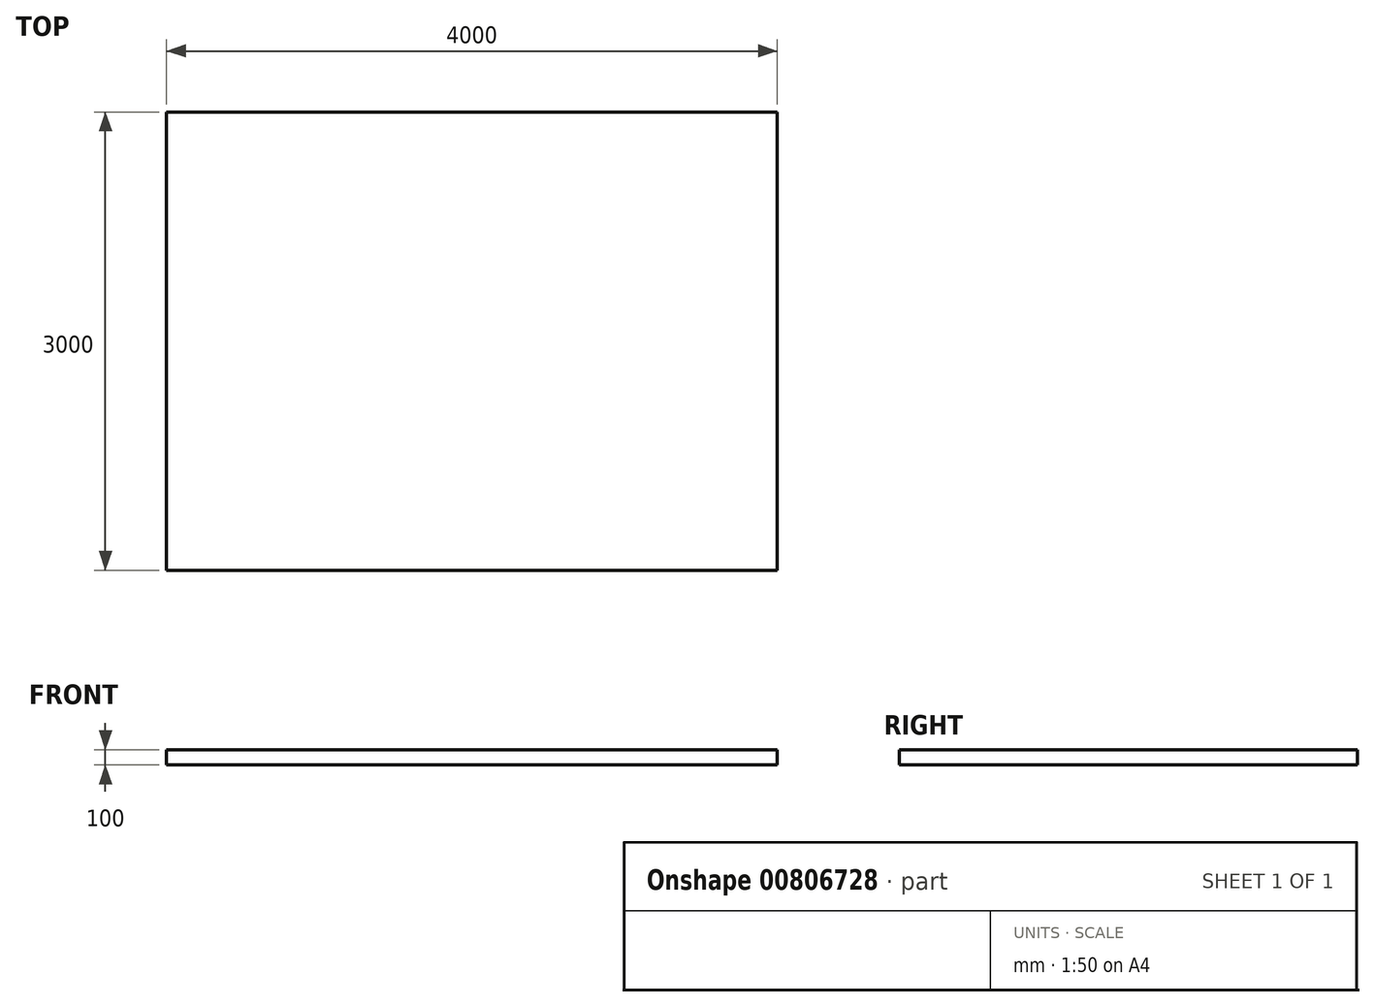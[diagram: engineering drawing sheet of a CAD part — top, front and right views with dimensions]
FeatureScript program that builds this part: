
annotation { "Feature Type Name" : "Feature", "Feature Type Description" : "" }
export const myFeature = defineFeature(function(context is Context, id is Id, definition is map)
    precondition{}
    {
        {
            var Q0;
            Q0=qCreatedBy(makeId("Top.planeOp"),FACE);
            var sketch = newSketch(context, id + "F0", { "sketchPlane" : qUnion([Q0])});
            skLineSegment(sketch, "E0.bottom", {"start": v(2000, -1500) * mm, "end": v(-2000, -1500) * mm});
            skLineSegment(sketch, "E0.top", {"start": v(2000, 1500) * mm, "end": v(-2000, 1500) * mm});
            skLineSegment(sketch, "E0.left", {"start": v(2000, -1500) * mm, "end": v(2000, 1500) * mm});
            skLineSegment(sketch, "E0.right", {"start": v(-2000, -1500) * mm, "end": v(-2000, 1500) * mm});
            skPoint(sketch, "E0.middle", {"position": v(0, 0) * mm});
            skSolve(sketch);
        }
        {
            var Q0;
            Q0=makeQuery(id+"F0.imprint","IMPRINT",FACE,{"disambiguationData":[TD([[makeQuery(id+"F0.imprint","IMPRINT",EDGE,{"derivedFrom":sQuery(id+"F0.wireOp",EDGE,"E0.bottom")}),-1.0]])]});
            extrude(context, id + "F1", {"entities" : qUnion([Q0]), "depth" : 100 * mm, "offsetDistance" : 25 * mm});
        }
    });
